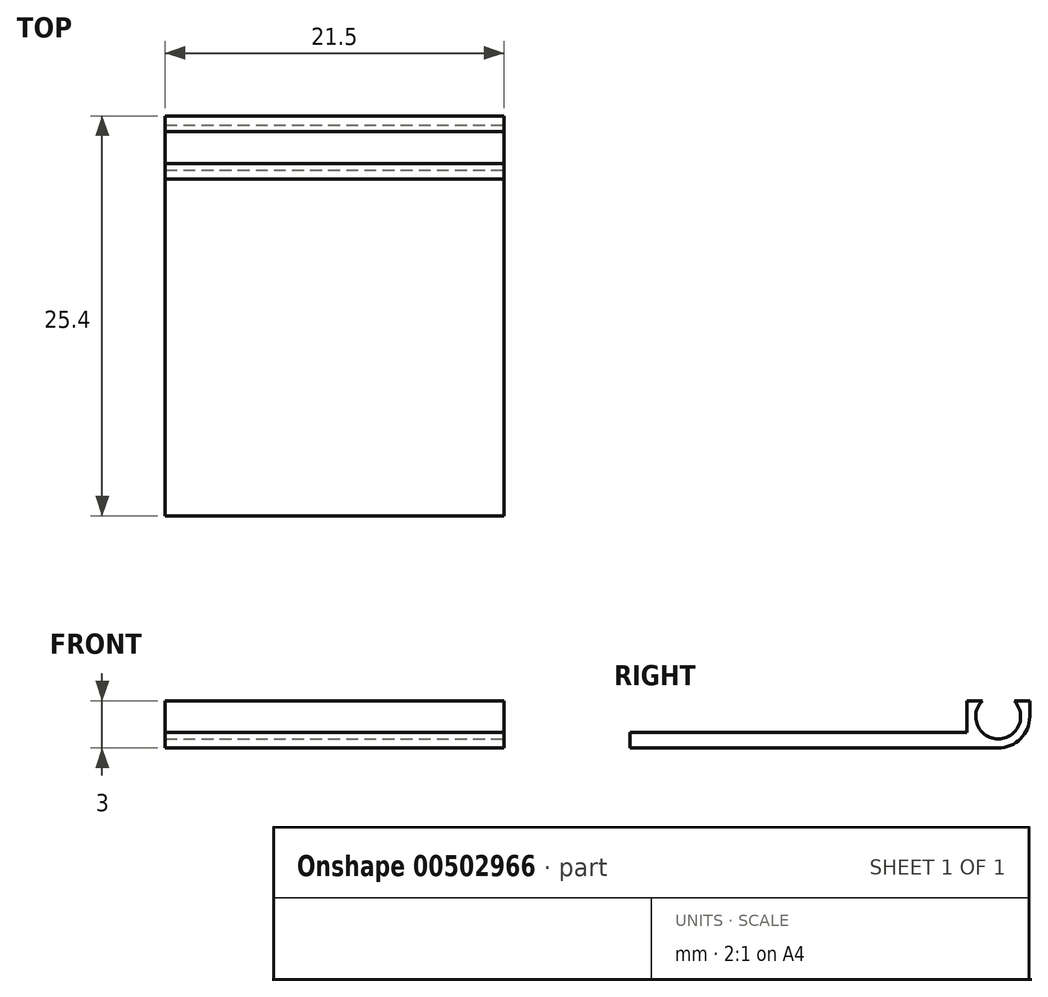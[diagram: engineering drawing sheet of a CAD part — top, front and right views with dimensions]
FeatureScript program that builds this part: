
annotation { "Feature Type Name" : "Feature", "Feature Type Description" : "" }
export const myFeature = defineFeature(function(context is Context, id is Id, definition is map)
    precondition{}
    {
        {
            var Q0;
            Q0=qCreatedBy(makeId("Top.planeOp"),FACE);
            var sketch = newSketch(context, id + "F0", { "sketchPlane" : qUnion([Q0])});
            skLineSegment(sketch, "E0.bottom", {"start": v(10.75, 10.7) * mm, "end": v(-10.75, 10.7) * mm});
            skLineSegment(sketch, "E0.top", {"start": v(10.75, -10.7) * mm, "end": v(-10.75, -10.7) * mm});
            skLineSegment(sketch, "E0.left", {"start": v(10.75, 10.7) * mm, "end": v(10.75, -10.7) * mm});
            skLineSegment(sketch, "E0.right", {"start": v(-10.75, 10.7) * mm, "end": v(-10.75, -10.7) * mm});
            skPoint(sketch, "E0.middle", {"position": v(0, 0) * mm});
            skLineSegment(sketch, "E1.top", {"start": v(10.75, 14.7) * mm, "end": v(-10.75, 14.7) * mm});
            skLineSegment(sketch, "E1.left", {"start": v(10.75, 10.7) * mm, "end": v(10.75, 14.7) * mm});
            skLineSegment(sketch, "E1.right", {"start": v(-10.75, 10.7) * mm, "end": v(-10.75, 14.7) * mm});
            skLineSegment(sketch, "E2.bottom", {"start": v(-10.75, -10.7) * mm, "end": v(10.75, -10.7) * mm});
            skSolve(sketch);
        }
        {
            var Q0;
            Q0=makeQuery(id+"F0.imprint","IMPRINT",FACE,{"disambiguationData":[TD([[makeQuery(id+"F0.imprint","IMPRINT",EDGE,{"derivedFrom":sQuery(id+"F0.wireOp",EDGE,"E0.left")}),-1.0]])]});
            extrude(context, id + "F1", {"entities" : qUnion([Q0]), "depth" : 1 * mm});
        }
        {
            var Q0;
            Q0=makeQuery(id+"F0.imprint","IMPRINT",FACE,{"disambiguationData":[TD([[makeQuery(id+"F0.imprint","IMPRINT",EDGE,{"derivedFrom":sQuery(id+"F0.wireOp",EDGE,"E0.bottom")}),-1.0]])]});
            var Q1;
            Q1=makeQuery(id+"F0.imprint","IMPRINT",FACE,{"disambiguationData":[TD([[makeQuery(id+"F0.imprint","IMPRINT",EDGE,{"derivedFrom":sQuery(id+"F0.wireOp",EDGE,"E2.bottom")}),-1.0]])]});
            extrude(context, id + "F2", {"entities" : qUnion([Q0, Q1]), "operationType" : NewBodyOperationType.ADD, "depth" : 3 * mm});
        }
        {
            var Q0;
            Q0=makeQuery(id+"F2.boolean.opBoolean","MERGE",FACE,{"derivedFrom":[makeQuery(id+"F1.opExtrude","SWEPT_FACE",FACE,{"disambiguationData":[OSD([sQuery(id+"F0.wireOp",EDGE,"E0.left")])]}),makeQuery(id+"F2.opExtrude","SWEPT_FACE",FACE,{"disambiguationData":[OSD([sQuery(id+"F0.wireOp",EDGE,"E1.left")])]}),makeQuery(id+"F2.opExtrude","SWEPT_FACE",FACE,{"disambiguationData":[OSD([sQuery(id+"F0.wireOp",EDGE,"E2.right")])]})]});
            var sketch = newSketch(context, id + "F3", { "sketchPlane" : qUnion([Q0])});
            skPoint(sketch, "E3", {"position": v(12.7, 2) * mm});
            skPoint(sketch, "E3.positionSnap0", {"position": v(12.7, 3) * mm});
            skSolve(sketch);
        }
        {
            var Q0;
            Q0=sQuery(id+"F3.wireOp",VERTEX,"E3");
            var Q1;
            Q1=sQuery(id+"F3.wireOp",VERTEX,"fdd9d276-48dd-46f6-a3d1-3cc48177e9de");
            var Q2;
            Q2=makeQuery(id+"F1.opExtrude","SWEPT_BODY",BODY,{"disambiguationData":[OSD([sQuery(id+"F0.wireOp",EDGE,"E0.left"),sQuery(id+"F0.wireOp",EDGE,"E0.right"),sQuery(id+"F0.wireOp",EDGE,"E0.bottom"),sQuery(id+"F0.wireOp",EDGE,"E2.bottom")])]});
            hole(context, id + "F4", {"style" : HoleStyle.SIMPLE, "endStyle" : HoleEndStyle.THROUGH, "holeDiameter" : 2.85 * mm, "isTappedThrough" : true, "tappedDepth" : 12 * mm, "tapClearance" : 3, "locations" : qUnion([Q0, Q1]), "scope" : qUnion([Q2])});
        }
        {
            var Q0;
            Q0=makeQuery(id+"F2.opExtrude","CAP_EDGE",EDGE,{"disambiguationData":[OSD([sQuery(id+"F0.wireOp",EDGE,"E1.top")])],"isStart":true});
            var Q1;
            Q1=makeQuery(id+"F2.opExtrude","CAP_EDGE",EDGE,{"disambiguationData":[OSD([sQuery(id+"F0.wireOp",EDGE,"E2.top")])],"isStart":true});
            fillet(context, id + "F5", {"entities" : qUnion([Q0, Q1]), "radius" : 2 * mm, "tangentPropagation" : true, "allowEdgeOverflow" : false});
        }
    });
